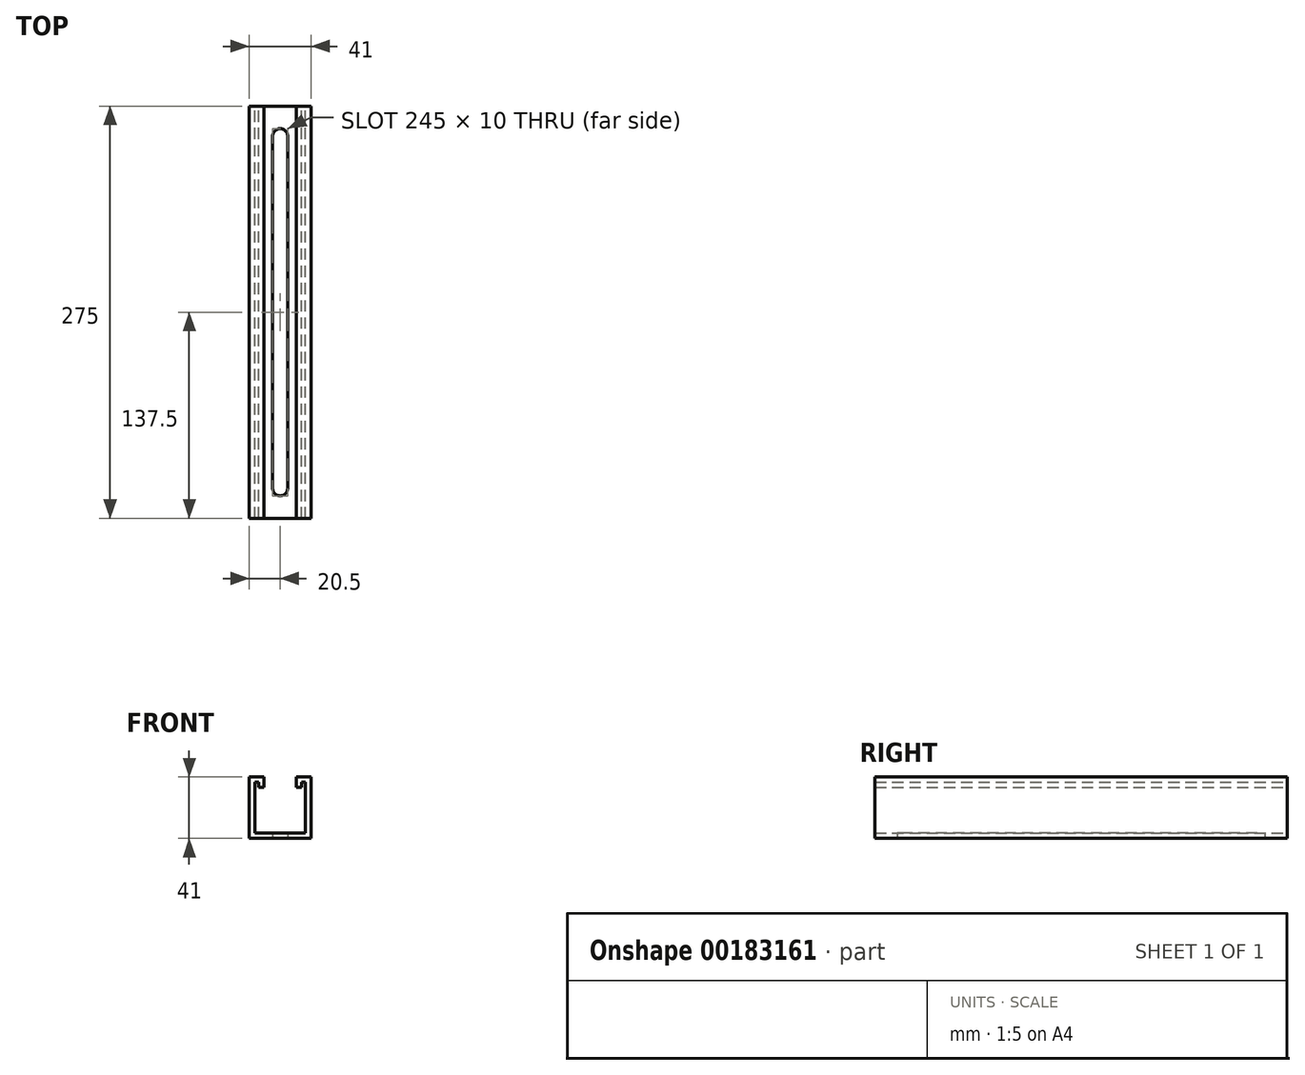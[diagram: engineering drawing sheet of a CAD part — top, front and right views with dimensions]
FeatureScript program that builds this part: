
annotation { "Feature Type Name" : "Feature", "Feature Type Description" : "" }
export const myFeature = defineFeature(function(context is Context, id is Id, definition is map)
    precondition{}
    {
        {
            var Q0;
            Q0=qCreatedBy(makeId("Front.planeOp"),FACE);
            var sketch = newSketch(context, id + "F0", { "sketchPlane" : qUnion([Q0])});
            skLineSegment(sketch, "E0", {"start": v(0, 0) * mm, "end": v(41, 0) * mm});
            skLineSegment(sketch, "E1", {"start": v(41, 0) * mm, "end": v(41, 41) * mm});
            skLineSegment(sketch, "E2", {"start": v(41, 41) * mm, "end": v(31.4, 41) * mm});
            skLineSegment(sketch, "E3", {"start": v(31.4, 41) * mm, "end": v(31.4, 34) * mm});
            skLineSegment(sketch, "E4", {"start": v(31.4, 34) * mm, "end": v(34.8, 34) * mm});
            skLineSegment(sketch, "E5", {"start": v(34.8, 34) * mm, "end": v(34.8, 37.5) * mm});
            skLineSegment(sketch, "E6", {"start": v(34.8, 37.5) * mm, "end": v(37.3, 37.5) * mm});
            skLineSegment(sketch, "E7", {"start": v(37.3, 37.5) * mm, "end": v(37.3, 3.7) * mm});
            skLineSegment(sketch, "E8", {"start": v(37.3, 3.7) * mm, "end": v(3.7, 3.7) * mm});
            skLineSegment(sketch, "E9", {"start": v(0, 0) * mm, "end": v(0, 41) * mm});
            skLineSegment(sketch, "E10", {"start": v(0, 41) * mm, "end": v(9.6, 41) * mm});
            skLineSegment(sketch, "E11", {"start": v(9.6, 41) * mm, "end": v(9.6, 34) * mm});
            skLineSegment(sketch, "E12", {"start": v(9.6, 34) * mm, "end": v(6.2, 34) * mm});
            skLineSegment(sketch, "E13", {"start": v(6.2, 34) * mm, "end": v(6.2, 37.5) * mm});
            skLineSegment(sketch, "E14", {"start": v(6.2, 37.5) * mm, "end": v(3.7, 37.5) * mm});
            skLineSegment(sketch, "E15", {"start": v(3.7, 37.5) * mm, "end": v(3.7, 3.7) * mm});
            skSolve(sketch);
        }
        {
            var Q0;
            Q0 = qSketchRegion(id + "F0", true);
            extrude(context, id + "F1", {"entities" : qUnion([Q0]), "depth" : 275 * mm});
        }
        {
            var Q0;
            Q0=makeQuery(id+"F1.opExtrude","SWEPT_FACE",FACE,{"disambiguationData":[OSD([sQuery(id+"F0.wireOp",EDGE,"E0")])]});
            var sketch = newSketch(context, id + "F2", { "sketchPlane" : qUnion([Q0])});
            skArc(sketch, "E16", {"start": v(15.5, 20) * mm, "mid": v(20.5, 15) * mm, "end": v(25.5, 20) * mm});
            skPoint(sketch, "E16.centerSnap0", {"position": v(20.5, 0) * mm});
            skArc(sketch, "E17", {"start": v(25.5, 255) * mm, "mid": v(20.5, 260) * mm, "end": v(15.5, 255) * mm});
            skPoint(sketch, "E17.centerSnap0", {"position": v(20.5, 275) * mm});
            skLineSegment(sketch, "E18", {"start": v(25.5, 20) * mm, "end": v(25.5, 255) * mm});
            skLineSegment(sketch, "E19", {"start": v(15.5, 255) * mm, "end": v(15.5, 20) * mm});
            skSolve(sketch);
        }
        {
            var Q0;
            Q0 = qSketchRegion(id + "F2", true);
            extrude(context, id + "F3", {"entities" : qUnion([Q0]), "operationType" : NewBodyOperationType.REMOVE, "endBound" : BoundingType.UP_TO_NEXT, "oppositeDirection" : true, "depth" : 25 * mm});
        }
    });
